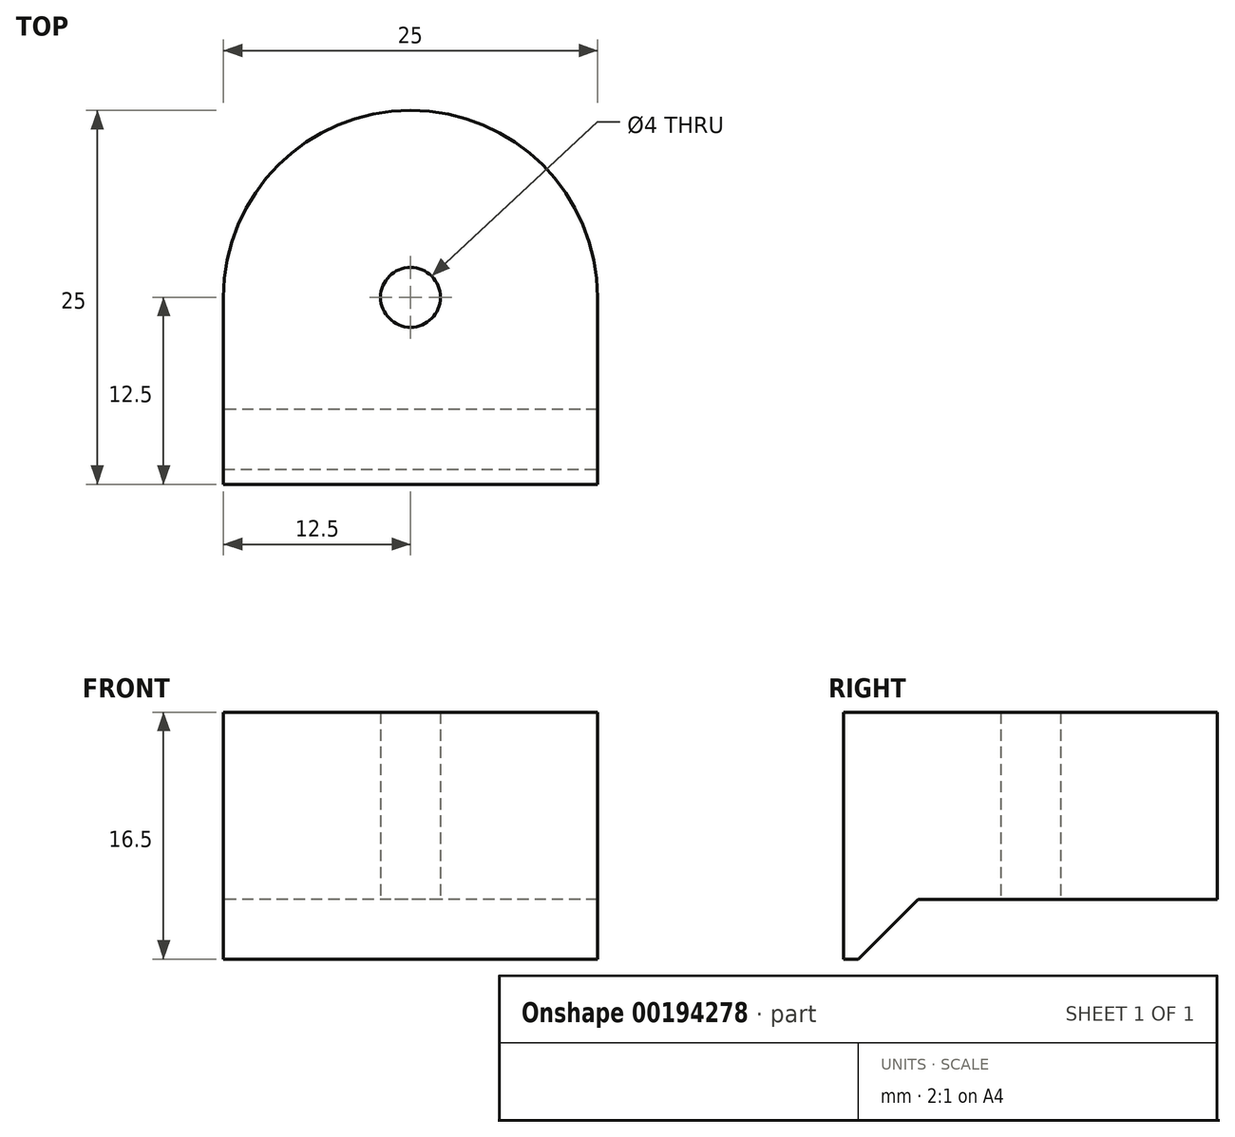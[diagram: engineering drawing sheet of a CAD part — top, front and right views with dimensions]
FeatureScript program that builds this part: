
annotation { "Feature Type Name" : "Feature", "Feature Type Description" : "" }
export const myFeature = defineFeature(function(context is Context, id is Id, definition is map)
    precondition{}
    {
        {
            assignVariable(context, id + "F0", {"name" : "minDepth", "anyValue" : 1.5});
        }
        {
            var Q0;
            Q0=qCreatedBy(makeId("Top.planeOp"),FACE);
            var sketch = newSketch(context, id + "F1", { "sketchPlane" : qUnion([Q0])});
            skCircle(sketch, "E0", {"center": v(0, 0) * mm, "radius": 12.5 * mm});
            skCircle(sketch, "E1", {"center": v(0, 0) * mm, "radius": 2 * mm});
            skLineSegment(sketch, "E2.bottom", {"start": v(12.5, -12.5) * mm, "end": v(-12.5, -12.5) * mm});
            skLineSegment(sketch, "E2.top", {"start": v(12.5, 12.5) * mm, "end": v(-12.5, 12.5) * mm});
            skLineSegment(sketch, "E2.left", {"start": v(12.5, -12.5) * mm, "end": v(12.5, 12.5) * mm});
            skLineSegment(sketch, "E2.right", {"start": v(-12.5, -12.5) * mm, "end": v(-12.5, 12.5) * mm});
            skLineSegment(sketch, "E3", {"start": v(-12.5, -11.5) * mm, "end": v(12.5, -11.5) * mm});
            skSolve(sketch);
        }
        {
            var Q0;
            {var subQ0=sQuery(id+"F1.wireOp",EDGE,"E2.right");var subQ1=sQuery(id+"F1.wireOp",EDGE,"E0");var subQ2=makeQuery(id+"F1.imprint","INTERSECT",VERTEX,{"derivedFrom":[subQ1,subQ0]});Q0=makeQuery(id+"F1.imprint","IMPRINT",FACE,{"disambiguationData":[TD([[makeQuery(id+"F1.imprint","IMPRINT",EDGE,{"disambiguationData":[TD([[subQ2,-1.0]])],"derivedFrom":subQ1}),-1.0]])]});}
            var Q1;
            Q1=makeQuery(id+"F1.imprint","IMPRINT",FACE,{"disambiguationData":[TD([[makeQuery(id+"F1.imprint","IMPRINT",EDGE,{"derivedFrom":sQuery(id+"F1.wireOp",EDGE,"E1")}),-1.0]])]});
            var Q2;
            {var subQ0=sQuery(id+"F1.wireOp",EDGE,"E2.left");var subQ1=sQuery(id+"F1.wireOp",EDGE,"E0");var subQ2=makeQuery(id+"F1.imprint","INTERSECT",VERTEX,{"derivedFrom":[subQ1,subQ0]});Q2=makeQuery(id+"F1.imprint","IMPRINT",FACE,{"disambiguationData":[TD([[makeQuery(id+"F1.imprint","IMPRINT",EDGE,{"disambiguationData":[TD([[subQ2,1.0]])],"derivedFrom":subQ1}),-1.0]])]});}
            var Q3;
            {var subQ0=sQuery(id+"F1.wireOp",EDGE,"E2.bottom");var subQ1=sQuery(id+"F1.wireOp",EDGE,"E0");var subQ2=makeQuery(id+"F1.imprint","INTERSECT",VERTEX,{"derivedFrom":[subQ1,subQ0]});Q3=makeQuery(id+"F1.imprint","IMPRINT",FACE,{"disambiguationData":[TD([[makeQuery(id+"F1.imprint","IMPRINT",EDGE,{"disambiguationData":[TD([[subQ2,1.0]])],"derivedFrom":subQ1}),-1.0]])]});}
            var Q4;
            {var subQ0=sQuery(id+"F1.wireOp",EDGE,"E0");var subQ1=makeQuery(id+"F1.imprint","INTERSECT",VERTEX,{"derivedFrom":[subQ0,sQuery(id+"F1.wireOp",EDGE,"E2.bottom")]});Q4=makeQuery(id+"F1.imprint","IMPRINT",FACE,{"disambiguationData":[TD([[makeQuery(id+"F1.imprint","IMPRINT",EDGE,{"disambiguationData":[TD([[subQ1,1.0]])],"derivedFrom":subQ0}),1.0]])]});}
            var Q5;
            {var subQ0=sQuery(id+"F1.wireOp",EDGE,"E2.bottom");var subQ1=sQuery(id+"F1.wireOp",EDGE,"E0");var subQ2=makeQuery(id+"F1.imprint","INTERSECT",VERTEX,{"derivedFrom":[subQ1,subQ0]});Q5=makeQuery(id+"F1.imprint","IMPRINT",FACE,{"disambiguationData":[TD([[makeQuery(id+"F1.imprint","IMPRINT",EDGE,{"disambiguationData":[TD([[subQ2,-1.0]])],"derivedFrom":subQ1}),-1.0]])]});}
            extrude(context, id + "F2", {"entities" : qUnion([Q0, Q1, Q2, Q3, Q4, Q5]), "depth" : 11 * mm});
        }
        {
            var Q0;
            {var subQ0=sQuery(id+"F1.wireOp",EDGE,"E2.bottom");var subQ1=sQuery(id+"F1.wireOp",EDGE,"E0");var subQ2=makeQuery(id+"F1.imprint","INTERSECT",VERTEX,{"derivedFrom":[subQ1,subQ0]});Q0=makeQuery(id+"F1.imprint","IMPRINT",FACE,{"disambiguationData":[TD([[makeQuery(id+"F1.imprint","IMPRINT",EDGE,{"disambiguationData":[TD([[subQ2,1.0]])],"derivedFrom":subQ1}),-1.0]])]});}
            var Q1;
            {var subQ0=sQuery(id+"F1.wireOp",EDGE,"E0");var subQ1=makeQuery(id+"F1.imprint","INTERSECT",VERTEX,{"derivedFrom":[subQ0,sQuery(id+"F1.wireOp",EDGE,"E2.bottom")]});Q1=makeQuery(id+"F1.imprint","IMPRINT",FACE,{"disambiguationData":[TD([[makeQuery(id+"F1.imprint","IMPRINT",EDGE,{"disambiguationData":[TD([[subQ1,1.0]])],"derivedFrom":subQ0}),1.0]])]});}
            var Q2;
            {var subQ0=sQuery(id+"F1.wireOp",EDGE,"E2.bottom");var subQ1=sQuery(id+"F1.wireOp",EDGE,"E0");var subQ2=makeQuery(id+"F1.imprint","INTERSECT",VERTEX,{"derivedFrom":[subQ1,subQ0]});Q2=makeQuery(id+"F1.imprint","IMPRINT",FACE,{"disambiguationData":[TD([[makeQuery(id+"F1.imprint","IMPRINT",EDGE,{"disambiguationData":[TD([[subQ2,-1.0]])],"derivedFrom":subQ1}),-1.0]])]});}
            var Q3;
            {var subQ0=sQuery(id+"F1.wireOp",EDGE,"E2.left");var subQ1=sQuery(id+"F1.wireOp",EDGE,"E0");var subQ2=makeQuery(id+"F1.imprint","INTERSECT",VERTEX,{"derivedFrom":[subQ1,subQ0]});Q3=makeQuery(id+"F1.imprint","IMPRINT",FACE,{"disambiguationData":[TD([[makeQuery(id+"F1.imprint","IMPRINT",EDGE,{"disambiguationData":[TD([[subQ2,1.0]])],"derivedFrom":subQ1}),-1.0]])]});}
            var Q4;
            Q4=makeQuery(id+"F1.imprint","IMPRINT",FACE,{"disambiguationData":[TD([[makeQuery(id+"F1.imprint","IMPRINT",EDGE,{"derivedFrom":sQuery(id+"F1.wireOp",EDGE,"E1")}),-1.0]])]});
            var Q5;
            {var subQ0=sQuery(id+"F1.wireOp",EDGE,"E2.right");var subQ1=sQuery(id+"F1.wireOp",EDGE,"E0");var subQ2=makeQuery(id+"F1.imprint","INTERSECT",VERTEX,{"derivedFrom":[subQ1,subQ0]});Q5=makeQuery(id+"F1.imprint","IMPRINT",FACE,{"disambiguationData":[TD([[makeQuery(id+"F1.imprint","IMPRINT",EDGE,{"disambiguationData":[TD([[subQ2,-1.0]])],"derivedFrom":subQ1}),-1.0]])]});}
            extrude(context, id + "F3", {"entities" : qUnion([Q0, Q1, Q2, Q3, Q4, Q5]), "oppositeDirection" : true, "depth" : (getVariable(context, 'minDepth')) * mm});
        }
        {
            assignVariable(context, id + "F4", {"name" : "lipHeight", "anyValue" : 4});
        }
        {
            var Q0;
            {var subQ0=sQuery(id+"F1.wireOp",EDGE,"E2.bottom");var subQ1=sQuery(id+"F1.wireOp",EDGE,"E0");var subQ2=makeQuery(id+"F1.imprint","INTERSECT",VERTEX,{"derivedFrom":[subQ1,subQ0]});Q0=makeQuery(id+"F1.imprint","IMPRINT",FACE,{"disambiguationData":[TD([[makeQuery(id+"F1.imprint","IMPRINT",EDGE,{"disambiguationData":[TD([[subQ2,1.0]])],"derivedFrom":subQ1}),-1.0]])]});}
            var Q1;
            {var subQ0=sQuery(id+"F1.wireOp",EDGE,"E0");var subQ1=makeQuery(id+"F1.imprint","INTERSECT",VERTEX,{"derivedFrom":[subQ0,sQuery(id+"F1.wireOp",EDGE,"E2.bottom")]});Q1=makeQuery(id+"F1.imprint","IMPRINT",FACE,{"disambiguationData":[TD([[makeQuery(id+"F1.imprint","IMPRINT",EDGE,{"disambiguationData":[TD([[subQ1,1.0]])],"derivedFrom":subQ0}),1.0]])]});}
            var Q2;
            {var subQ0=sQuery(id+"F1.wireOp",EDGE,"E2.bottom");var subQ1=sQuery(id+"F1.wireOp",EDGE,"E0");var subQ2=makeQuery(id+"F1.imprint","INTERSECT",VERTEX,{"derivedFrom":[subQ1,subQ0]});Q2=makeQuery(id+"F1.imprint","IMPRINT",FACE,{"disambiguationData":[TD([[makeQuery(id+"F1.imprint","IMPRINT",EDGE,{"disambiguationData":[TD([[subQ2,-1.0]])],"derivedFrom":subQ1}),-1.0]])]});}
            extrude(context, id + "F5", {"entities" : qUnion([Q0, Q1, Q2]), "operationType" : NewBodyOperationType.ADD, "oppositeDirection" : true, "depth" : (getVariable(context, 'lipHeight') + getVariable(context, 'minDepth')) * mm});
        }
        {
            var Q0;
            Q0=makeQuery(id+"F5.boolean.opBoolean","INTERSECT",EDGE,{"derivedFrom":[makeQuery(id+"F3.opExtrude","CAP_FACE",FACE,{"disambiguationData":[OSD([sQuery(id+"F1.wireOp",EDGE,"E0"),sQuery(id+"F1.wireOp",EDGE,"E1"),sQuery(id+"F1.wireOp",EDGE,"E2.bottom"),sQuery(id+"F1.wireOp",EDGE,"E2.left"),sQuery(id+"F1.wireOp",EDGE,"E2.right")])],"isStart":false}),makeQuery(id+"F5.opExtrude","SWEPT_FACE",FACE,{"disambiguationData":[OSD([sQuery(id+"F1.wireOp",EDGE,"E3")])]})]});
            chamfer(context, id + "F6", {"entities" : qUnion([Q0]), "width" : (getVariable(context, 'lipHeight')) * mm, "tangentPropagation" : true});
        }
    });
